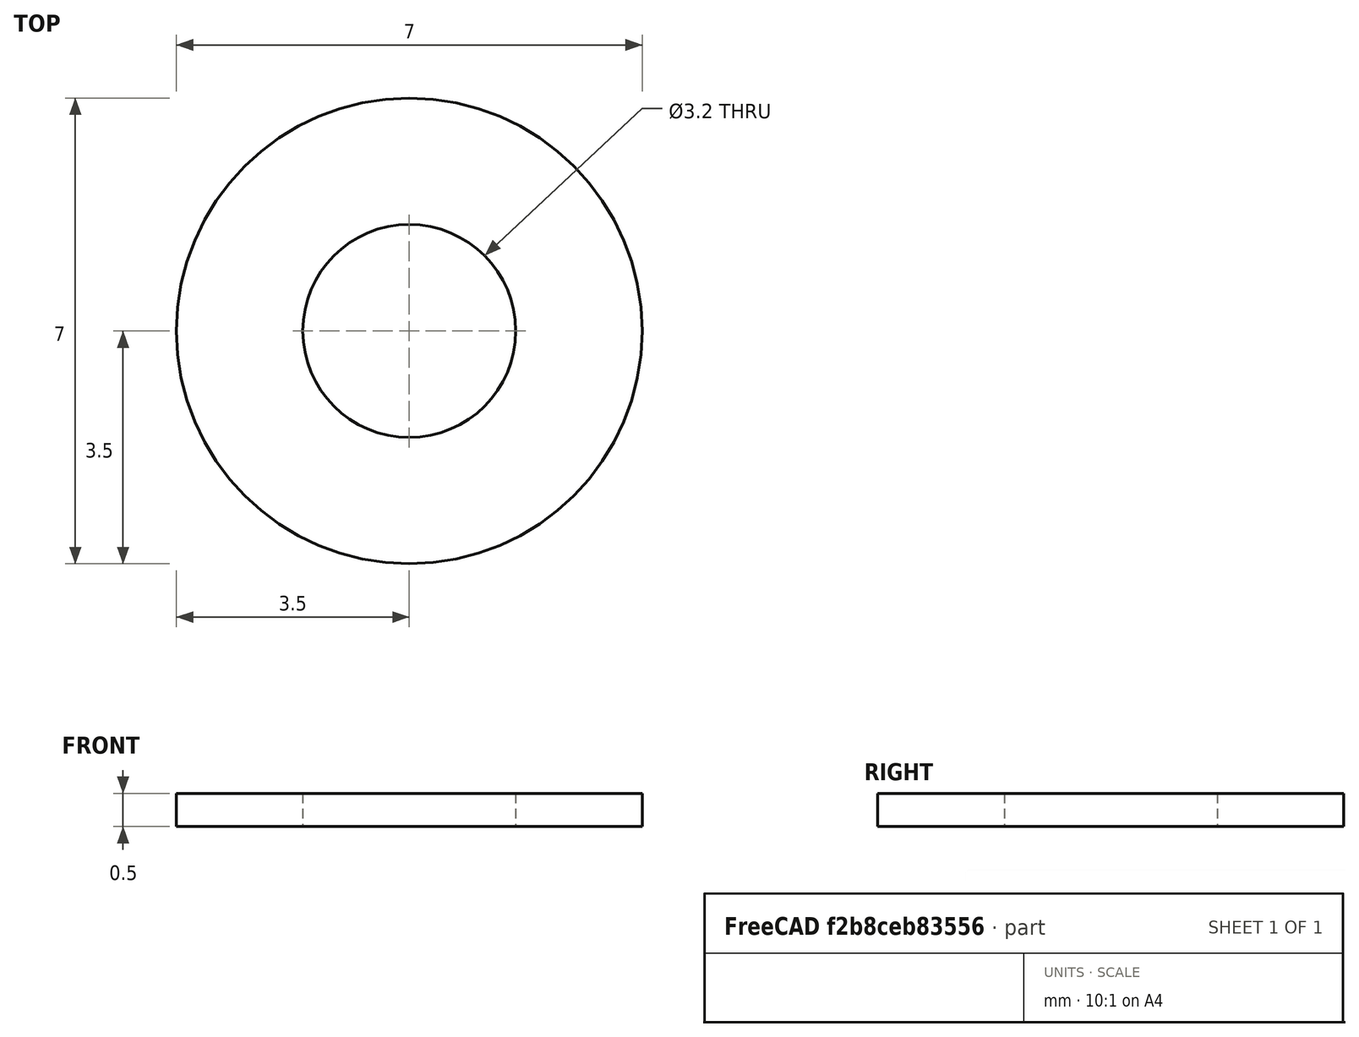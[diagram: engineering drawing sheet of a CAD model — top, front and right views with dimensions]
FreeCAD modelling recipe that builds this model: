
FCSTD DOCUMENT  (FreeCAD 0.14R3700 (Git))
Label: Scheibe DIN 125 - A 3,2
License: CC-BY 3.0
LicenseURL: http://creativecommons.org/licenses/by/3.0/
objects: Sketcher::SketchObject×1, PartDesign::Revolution×1, Part::Feature×1
note: 4 computed .brp shape members not serialized (recipe doc carries the construction recipe); baked Part::Feature solids carry a one-line shape summary decoded from their .brp

FEATURE [Sketcher::SketchObject] Sketch
  Placement = pos=(0,0,0) rot=(0.57735,0.57735,0.57735;2.0944rad)
  sketch-geometry (4):
    g0: LineSegment StartX=1.6 StartY=0 StartZ=0 EndX=3.5 EndY=0 EndZ=0
    g1: LineSegment StartX=3.5 StartY=0 StartZ=0 EndX=3.5 EndY=0.5 EndZ=0
    g2: LineSegment StartX=3.5 StartY=0.5 StartZ=0 EndX=1.6 EndY=0.5 EndZ=0
    g3: LineSegment StartX=1.6 StartY=0.5 StartZ=0 EndX=1.6 EndY=0 EndZ=0
  constraints (12):
    c: Coincident(g0,g1)
    c: Coincident(g1,g2)
    c: Coincident(g2,g3)
    c: Coincident(g3,g0)
    c: Horizontal(g0)
    c: Horizontal(g2)
    c: Vertical(g1)
    c: Vertical(g3)
    c: PointOnObject(g0,g-1)
    c: DistanceY(g1) = 0.5
    c: DistanceX(g-1,g2) = 1.6
    c: DistanceX(g-1,g1) = 3.5
FEATURE [PartDesign::Revolution] Revolution  label="Scheibe DIN 125 - A 3,2 #"
  Angle = 360
  Axis = (0,0,1)
  Base = (0,0,0)
  Placement = pos=(0,0,0) rot=(0.57735,0.57735,0.57735;2.0944rad)
  ReferenceAxis = -> Sketch [V_Axis]
  Reversed = true
  Sketch = -> Sketch
FEATURE [Part::Feature] Revolution001  label="Scheibe DIN 125 - A 3,2 #001"
  Placement = pos=(0,0,0) rot=(0.57735,0.57735,0.57735;2.0944rad)
  shape: bbox 7 x 7 x 0.5 mm, 4 faces (baked)
